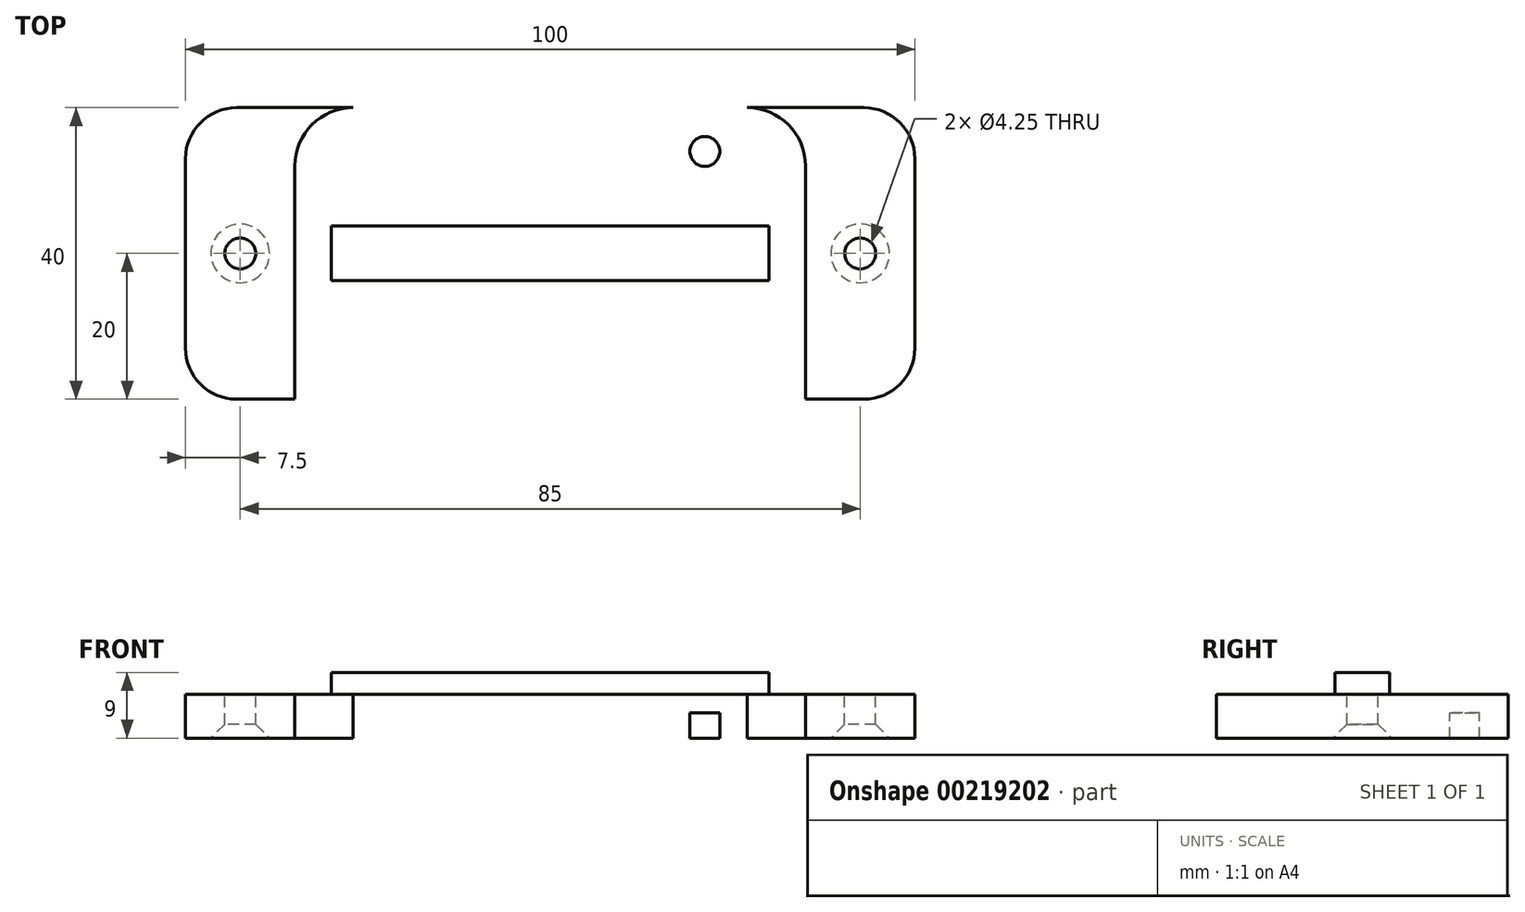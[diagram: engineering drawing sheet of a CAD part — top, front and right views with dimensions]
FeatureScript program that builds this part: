
annotation { "Feature Type Name" : "Feature", "Feature Type Description" : "" }
export const myFeature = defineFeature(function(context is Context, id is Id, definition is map)
    precondition{}
    {
        {
            var Q0;
            Q0=qCreatedBy(makeId("Top.planeOp"),FACE);
            var sketch = newSketch(context, id + "F0", { "sketchPlane" : qUnion([Q0])});
            skLineSegment(sketch, "E0.bottom", {"start": v(27, 35) * mm, "end": v(-27, 35) * mm});
            skLineSegment(sketch, "E0.top", {"start": v(27, -35) * mm, "end": v(-27, -35) * mm});
            skLineSegment(sketch, "E0.left", {"start": v(35, 27) * mm, "end": v(35, -27) * mm});
            skLineSegment(sketch, "E0.right", {"start": v(-35, 27) * mm, "end": v(-35, -27) * mm});
            skPoint(sketch, "E0.middle", {"position": v(0, 0) * mm});
            skPoint(sketch, "E1.visualSharp", {"position": v(-35, 35) * mm});
            skArc(sketch, "E1.filletArc", {"start": v(-27, 35) * mm, "mid": v(-32.66, 32.66) * mm, "end": v(-35, 27) * mm});
            skPoint(sketch, "E2.visualSharp", {"position": v(35, 35) * mm});
            skArc(sketch, "E2.filletArc", {"start": v(35, 27) * mm, "mid": v(32.66, 32.66) * mm, "end": v(27, 35) * mm});
            skPoint(sketch, "E3.visualSharp", {"position": v(35, -35) * mm});
            skArc(sketch, "E3.filletArc", {"start": v(27, -35) * mm, "mid": v(32.66, -32.66) * mm, "end": v(35, -27) * mm});
            skPoint(sketch, "E4.visualSharp", {"position": v(-35, -35) * mm});
            skArc(sketch, "E4.filletArc", {"start": v(-35, -27) * mm, "mid": v(-32.66, -32.66) * mm, "end": v(-27, -35) * mm});
            skLineSegment(sketch, "E5.bottom", {"start": v(21.2, 29) * mm, "end": v(-21.2, 29) * mm, "construction": true});
            skLineSegment(sketch, "E5.top", {"start": v(21.2, -29) * mm, "end": v(-21.2, -29) * mm, "construction": true});
            skLineSegment(sketch, "E5.left", {"start": v(21.2, 29) * mm, "end": v(21.2, -29) * mm, "construction": true});
            skLineSegment(sketch, "E5.right", {"start": v(-21.2, 29) * mm, "end": v(-21.2, -29) * mm, "construction": true});
            skCircle(sketch, "E6", {"center": v(-21.2, 29) * mm, "radius": 2.05 * mm});
            skCircle(sketch, "E7.MirrorC", {"center": v(21.2, 29) * mm, "radius": 2.05 * mm});
            skCircle(sketch, "E8.MirrorC", {"center": v(21.2, -29) * mm, "radius": 2.05 * mm});
            skCircle(sketch, "E9.MirrorC", {"center": v(-21.2, -29) * mm, "radius": 2.05 * mm});
            skSolve(sketch);
        }
        {
            var Q0;
            Q0=makeQuery(id+"F0.imprint","IMPRINT",FACE,{"disambiguationData":[TD([[makeQuery(id+"F0.imprint","IMPRINT",EDGE,{"derivedFrom":sQuery(id+"F0.wireOp",EDGE,"ECZ0KXlq-rXvm-XOFO-M0kJ-3CG6qAbGzwhK.left")}),-1.0]])]});
            var Q1;
            Q1=makeQuery(id+"F0.imprint","IMPRINT",FACE,{"disambiguationData":[TD([[makeQuery(id+"F0.imprint","IMPRINT",EDGE,{"derivedFrom":sQuery(id+"F0.wireOp",EDGE,"1wAoUNru-vWGU-2yXA-mhRa-oQ9e8RuAtVco.bottom")}),1.0]])]});
            var Q2;
            Q2=makeQuery(id+"F0.imprint","IMPRINT",FACE,{"disambiguationData":[TD([[makeQuery(id+"F0.imprint","IMPRINT",EDGE,{"derivedFrom":sQuery(id+"F0.wireOp",EDGE,"ECZ0KXlq-rXvm-XOFO-M0kJ-3CG6qAbGzwhK.right")}),1.0]])]});
            var Q3;
            Q3=makeQuery(id+"F0.imprint","IMPRINT",FACE,{"disambiguationData":[TD([[makeQuery(id+"F0.imprint","IMPRINT",EDGE,{"derivedFrom":sQuery(id+"F0.wireOp",EDGE,"E0.bottom")}),1.0]])]});
            var Q4;
            Q4=makeQuery(id+"F0.imprint","IMPRINT",FACE,{"disambiguationData":[TD([[makeQuery(id+"F0.imprint","IMPRINT",EDGE,{"derivedFrom":sQuery(id+"F0.wireOp",EDGE,"E0.top")}),-1.0]])]});
            var Q5;
            Q5=makeQuery(id+"F0.imprint","IMPRINT",FACE,{"disambiguationData":[TD([[makeQuery(id+"F0.imprint","IMPRINT",EDGE,{"derivedFrom":sQuery(id+"F0.wireOp",EDGE,"1wAoUNru-vWGU-2yXA-mhRa-oQ9e8RuAtVco.bottom")}),-1.0]])]});
            var Q6;
            Q6=makeQuery(id+"F0.imprint","IMPRINT",FACE,{"disambiguationData":[TD([[makeQuery(id+"F0.imprint","IMPRINT",EDGE,{"derivedFrom":sQuery(id+"F0.wireOp",EDGE,"E6")}),1.0]])]});
            var Q7;
            Q7=makeQuery(id+"F0.imprint","IMPRINT",FACE,{"disambiguationData":[TD([[makeQuery(id+"F0.imprint","IMPRINT",EDGE,{"derivedFrom":sQuery(id+"F0.wireOp",EDGE,"E7.MirrorC")}),-1.0]])]});
            var Q8;
            Q8=makeQuery(id+"F0.imprint","IMPRINT",FACE,{"disambiguationData":[TD([[makeQuery(id+"F0.imprint","IMPRINT",EDGE,{"derivedFrom":sQuery(id+"F0.wireOp",EDGE,"E8.MirrorC")}),1.0]])]});
            var Q9;
            Q9=makeQuery(id+"F0.imprint","IMPRINT",FACE,{"disambiguationData":[TD([[makeQuery(id+"F0.imprint","IMPRINT",EDGE,{"derivedFrom":sQuery(id+"F0.wireOp",EDGE,"E9.MirrorC")}),-1.0]])]});
            extrude(context, id + "F1", {"entities" : qUnion([Q0, Q1, Q2, Q3, Q4, Q5, Q6, Q7, Q8, Q9]), "oppositeDirection" : true, "depth" : 6 * mm});
        }
        {
            var Q0;
            Q0=qCreatedBy(makeId("Top.planeOp"),FACE);
            var sketch = newSketch(context, id + "F2", { "sketchPlane" : qUnion([Q0])});
            skCircle(sketch, "E10", {"center": v(-42.5, 15) * mm, "radius": 2.12 * mm});
            skLineSegment(sketch, "E11.bottom", {"start": v(43, 35) * mm, "end": v(-43, 35) * mm});
            skLineSegment(sketch, "E11.top", {"start": v(43, -5) * mm, "end": v(-43, -5) * mm});
            skLineSegment(sketch, "E11.left", {"start": v(50, 28) * mm, "end": v(50, 2) * mm});
            skLineSegment(sketch, "E11.right", {"start": v(-50, 28) * mm, "end": v(-50, 2) * mm});
            skPoint(sketch, "E11.middle", {"position": v(0, 15) * mm});
            skPoint(sketch, "E12", {"position": v(-50, 15) * mm});
            skPoint(sketch, "E13.visualSharp", {"position": v(-50, 35) * mm});
            skArc(sketch, "E13.filletArc", {"start": v(-43, 35) * mm, "mid": v(-47.95, 32.95) * mm, "end": v(-50, 28) * mm});
            skPoint(sketch, "E14.visualSharp", {"position": v(50, 35) * mm});
            skArc(sketch, "E14.filletArc", {"start": v(50, 28) * mm, "mid": v(47.95, 32.95) * mm, "end": v(43, 35) * mm});
            skPoint(sketch, "E15.visualSharp", {"position": v(50, -5) * mm});
            skArc(sketch, "E15.filletArc", {"start": v(43, -5) * mm, "mid": v(47.95, -2.95) * mm, "end": v(50, 2) * mm});
            skPoint(sketch, "E16.visualSharp", {"position": v(-50, -5) * mm});
            skArc(sketch, "E16.filletArc", {"start": v(-50, 2) * mm, "mid": v(-47.95, -2.95) * mm, "end": v(-43, -5) * mm});
            skCircle(sketch, "E17.MirrorC", {"center": v(42.5, 15) * mm, "radius": 2.12 * mm});
            skLineSegment(sketch, "E18.bottom", {"start": v(30, 18.75) * mm, "end": v(-30, 18.75) * mm});
            skLineSegment(sketch, "E18.top", {"start": v(30, 11.25) * mm, "end": v(-30, 11.25) * mm});
            skLineSegment(sketch, "E18.left", {"start": v(30, 18.75) * mm, "end": v(30, 11.25) * mm});
            skLineSegment(sketch, "E18.right", {"start": v(-30, 18.75) * mm, "end": v(-30, 11.25) * mm});
            skSolve(sketch);
        }
        {
            var Q0;
            Q0=makeQuery(id+"F2.imprint","IMPRINT",FACE,{"disambiguationData":[TD([[makeQuery(id+"F2.imprint","IMPRINT",EDGE,{"derivedFrom":sQuery(id+"F2.wireOp",EDGE,"E10")}),-1.0]])]});
            var Q1;
            Q1 = qSketchRegion(id + "F2", true);
            extrude(context, id + "F3", {"entities" : qUnion([Q0, Q1]), "operationType" : NewBodyOperationType.ADD, "oppositeDirection" : true, "depth" : 6 * mm});
        }
        {
            var Q0;
            Q0=qCreatedBy(makeId("Top.planeOp"),FACE);
            var sketch = newSketch(context, id + "F4", { "sketchPlane" : qUnion([Q0])});
            skCircle(sketch, "E19.cCircle", {"center": v(21.15, -29.06) * mm, "radius": 3.5 * mm, "construction": true});
            skLineSegment(sketch, "E19.0", {"start": v(23.17, -32.56) * mm, "end": v(19.13, -32.56) * mm});
            skLineSegment(sketch, "E19.1", {"start": v(19.13, -32.56) * mm, "end": v(17.1, -29.06) * mm});
            skLineSegment(sketch, "E19.2", {"start": v(17.1, -29.06) * mm, "end": v(19.13, -25.56) * mm});
            skLineSegment(sketch, "E19.3", {"start": v(19.13, -25.56) * mm, "end": v(23.17, -25.56) * mm});
            skLineSegment(sketch, "E19.4", {"start": v(23.17, -25.56) * mm, "end": v(25.2, -29.06) * mm});
            skLineSegment(sketch, "E19.5", {"start": v(25.2, -29.06) * mm, "end": v(23.17, -32.56) * mm});
            skPoint(sketch, "E19.0.midPoint", {"position": v(21.15, -32.56) * mm});
            skLineSegment(sketch, "E20.MirrorCS", {"start": v(-19.13, -25.56) * mm, "end": v(-23.17, -25.56) * mm});
            skLineSegment(sketch, "E21.MirrorCS", {"start": v(-17.1, -29.06) * mm, "end": v(-19.13, -25.56) * mm});
            skLineSegment(sketch, "E22.MirrorCS", {"start": v(-19.13, -32.56) * mm, "end": v(-17.1, -29.06) * mm});
            skLineSegment(sketch, "E23.MirrorCS", {"start": v(-23.17, -32.56) * mm, "end": v(-19.13, -32.56) * mm});
            skLineSegment(sketch, "E24.MirrorCS", {"start": v(-25.2, -29.06) * mm, "end": v(-23.17, -32.56) * mm});
            skLineSegment(sketch, "E25.MirrorCS", {"start": v(-23.17, -25.56) * mm, "end": v(-25.2, -29.06) * mm});
            skLineSegment(sketch, "E26.MirrorCS", {"start": v(-19.13, 25.56) * mm, "end": v(-23.17, 25.56) * mm});
            skLineSegment(sketch, "E27.MirrorCS", {"start": v(-23.17, 25.56) * mm, "end": v(-25.2, 29.06) * mm});
            skLineSegment(sketch, "E28.MirrorCS", {"start": v(-25.2, 29.06) * mm, "end": v(-23.17, 32.56) * mm});
            skLineSegment(sketch, "E29.MirrorCS", {"start": v(-23.17, 32.56) * mm, "end": v(-19.13, 32.56) * mm});
            skLineSegment(sketch, "E30.MirrorCS", {"start": v(-19.13, 32.56) * mm, "end": v(-17.1, 29.06) * mm});
            skLineSegment(sketch, "E31.MirrorCS", {"start": v(-17.1, 29.06) * mm, "end": v(-19.13, 25.56) * mm});
            skLineSegment(sketch, "E32.MirrorCS", {"start": v(17.1, 29.06) * mm, "end": v(19.13, 25.56) * mm});
            skLineSegment(sketch, "E33.MirrorCS", {"start": v(19.13, 32.56) * mm, "end": v(17.1, 29.06) * mm});
            skLineSegment(sketch, "E34.MirrorCS", {"start": v(23.17, 32.56) * mm, "end": v(19.13, 32.56) * mm});
            skLineSegment(sketch, "E35.MirrorCS", {"start": v(25.2, 29.06) * mm, "end": v(23.17, 32.56) * mm});
            skLineSegment(sketch, "E36.MirrorCS", {"start": v(23.17, 25.56) * mm, "end": v(25.2, 29.06) * mm});
            skLineSegment(sketch, "E37.MirrorCS", {"start": v(19.13, 25.56) * mm, "end": v(23.17, 25.56) * mm});
            skCircle(sketch, "E38.MirrorC", {"center": v(21.15, 29.06) * mm, "radius": 3.5 * mm, "construction": true});
            skSolve(sketch);
        }
        {
            var Q0;
            Q0=makeQuery(id+"F4.imprint","IMPRINT",FACE,{"disambiguationData":[TD([[makeQuery(id+"F4.imprint","IMPRINT",EDGE,{"derivedFrom":sQuery(id+"F4.wireOp",EDGE,"E19.0")}),-1.0]])]});
            var Q1;
            Q1=makeQuery(id+"F4.imprint","IMPRINT",FACE,{"disambiguationData":[TD([[makeQuery(id+"F4.imprint","IMPRINT",EDGE,{"derivedFrom":sQuery(id+"F4.wireOp",EDGE,"E20.MirrorCS")}),1.0]])]});
            var Q2;
            Q2=makeQuery(id+"F4.imprint","IMPRINT",FACE,{"disambiguationData":[TD([[makeQuery(id+"F4.imprint","IMPRINT",EDGE,{"derivedFrom":sQuery(id+"F4.wireOp",EDGE,"E26.MirrorCS")}),-1.0]])]});
            var Q3;
            Q3=makeQuery(id+"F4.imprint","IMPRINT",FACE,{"disambiguationData":[TD([[makeQuery(id+"F4.imprint","IMPRINT",EDGE,{"derivedFrom":sQuery(id+"F4.wireOp",EDGE,"E32.MirrorCS")}),1.0]])]});
            extrude(context, id + "F5", {"entities" : qUnion([Q0, Q1, Q2, Q3]), "operationType" : NewBodyOperationType.REMOVE, "oppositeDirection" : true, "depth" : 2.5 * mm});
        }
        {
            var Q0;
            Q0=makeQuery(id+"F0.imprint","IMPRINT",FACE,{"disambiguationData":[TD([[makeQuery(id+"F0.imprint","IMPRINT",EDGE,{"derivedFrom":sQuery(id+"F0.wireOp",EDGE,"E6")}),1.0]])]});
            var Q1;
            Q1=makeQuery(id+"F0.imprint","IMPRINT",FACE,{"disambiguationData":[TD([[makeQuery(id+"F0.imprint","IMPRINT",EDGE,{"derivedFrom":sQuery(id+"F0.wireOp",EDGE,"E7.MirrorC")}),-1.0]])]});
            var Q2;
            Q2=makeQuery(id+"F0.imprint","IMPRINT",FACE,{"disambiguationData":[TD([[makeQuery(id+"F0.imprint","IMPRINT",EDGE,{"derivedFrom":sQuery(id+"F0.wireOp",EDGE,"E8.MirrorC")}),1.0]])]});
            var Q3;
            Q3=makeQuery(id+"F0.imprint","IMPRINT",FACE,{"disambiguationData":[TD([[makeQuery(id+"F0.imprint","IMPRINT",EDGE,{"derivedFrom":sQuery(id+"F0.wireOp",EDGE,"E9.MirrorC")}),-1.0]])]});
            extrude(context, id + "F6", {"entities" : qUnion([Q0, Q1, Q2, Q3]), "operationType" : NewBodyOperationType.REMOVE, "oppositeDirection" : true, "depth" : 25 * mm});
        }
        {
            var Q0;
            Q0=makeQuery(id+"F3.opExtrude","CAP_EDGE",EDGE,{"disambiguationData":[OSD([sQuery(id+"F2.wireOp",EDGE,"E17.MirrorC")])],"isStart":false});
            var Q1;
            Q1=makeQuery(id+"F3.opExtrude","CAP_EDGE",EDGE,{"disambiguationData":[OSD([sQuery(id+"F2.wireOp",EDGE,"E10")])],"isStart":false});
            chamfer(context, id + "F7", {"entities" : qUnion([Q0, Q1]), "width" : 1.9 * mm, "tangentPropagation" : true});
        }
        {
            var Q0;
            Q0=makeQuery(id+"F2.imprint","IMPRINT",FACE,{"disambiguationData":[TD([[makeQuery(id+"F2.imprint","IMPRINT",EDGE,{"derivedFrom":sQuery(id+"F2.wireOp",EDGE,"E18.bottom")}),1.0]])]});
            extrude(context, id + "F8", {"entities" : qUnion([Q0]), "operationType" : NewBodyOperationType.ADD, "depth" : 3 * mm});
        }
        {
            var Q0;
            Q0=qCreatedBy(makeId("Top.planeOp"),FACE);
            var sketch = newSketch(context, id + "F9", { "sketchPlane" : qUnion([Q0])});
            skCircle(sketch, "E39", {"center": v(0, -11) * mm, "radius": 17.5 * mm});
            skSolve(sketch);
        }
        {
            var Q0;
            Q0 = qSketchRegion(id + "F9", true);
            extrude(context, id + "F10", {"entities" : qUnion([Q0]), "operationType" : NewBodyOperationType.REMOVE, "oppositeDirection" : true, "depth" : 25 * mm});
        }
    });
